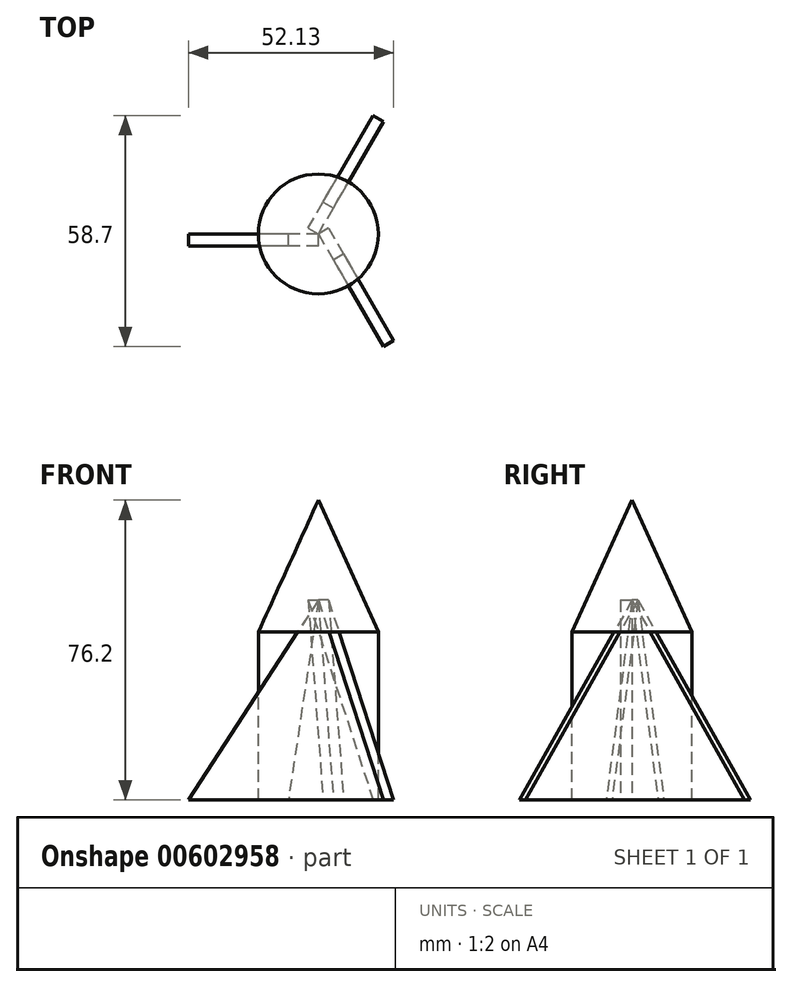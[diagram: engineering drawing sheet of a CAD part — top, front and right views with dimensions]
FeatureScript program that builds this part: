
annotation { "Feature Type Name" : "Feature", "Feature Type Description" : "" }
export const myFeature = defineFeature(function(context is Context, id is Id, definition is map)
    precondition{}
    {
        {
            var Q0;
            Q0=qCreatedBy(makeId("Front.planeOp"),FACE);
            var sketch = newSketch(context, id + "F0", { "sketchPlane" : qUnion([Q0])});
            skLineSegment(sketch, "E0", {"start": v(-15.24, 42.64) * mm, "end": v(-15.24, 0) * mm});
            skLineSegment(sketch, "E1", {"start": v(-15.24, 42.64) * mm, "end": v(0, 76.2) * mm});
            skLineSegment(sketch, "E2", {"start": v(0, 76.2) * mm, "end": v(0, 0) * mm});
            skLineSegment(sketch, "E3", {"start": v(-15.24, 0) * mm, "end": v(0, 0) * mm});
            skSolve(sketch);
        }
        {
            var Q0;
            Q0=makeQuery(id+"F0.imprint","IMPRINT",FACE,{"disambiguationData":[TD([[makeQuery(id+"F0.imprint","IMPRINT",EDGE,{"derivedFrom":sQuery(id+"F0.wireOp",EDGE,"E0")}),1.0]])]});
            var Q1;
            Q1=sQuery(id+"F0.wireOp",EDGE,"E2");
            revolve(context, id + "F1", {"entities" : qUnion([Q0]), "axis" : qUnion([Q1]), "revolveType" : RevolveType.FULL});
        }
        {
            var Q0;
            Q0=qCreatedBy(makeId("Front.planeOp"),FACE);
            var sketch = newSketch(context, id + "F2", { "sketchPlane" : qUnion([Q0])});
            skLineSegment(sketch, "E4", {"start": v(0, -12.68) * mm, "end": v(0, 76.93) * mm, "construction": true});
            skSolve(sketch);
        }
        {
            var Q0;
            Q0=qCreatedBy(makeId("Front.planeOp"),FACE);
            var sketch = newSketch(context, id + "F3", { "sketchPlane" : qUnion([Q0])});
            skLineSegment(sketch, "E5", {"start": v(0, 50.78) * mm, "end": v(-33.02, 0) * mm});
            skLineSegment(sketch, "E6", {"start": v(-7.62, 0) * mm, "end": v(-33.02, 0) * mm});
            skLineSegment(sketch, "E7", {"start": v(0, 50.78) * mm, "end": v(-7.62, 0) * mm});
            skSolve(sketch);
        }
        {
            var Q0;
            Q0=makeQuery(id+"F3.imprint","IMPRINT",FACE,{"disambiguationData":[TD([[makeQuery(id+"F3.imprint","IMPRINT",EDGE,{"derivedFrom":sQuery(id+"F3.wireOp",EDGE,"E5")}),1.0]])]});
            extrude(context, id + "F4", {"entities" : qUnion([Q0]), "depth" : 3 * mm, "offsetDistance" : 25.4 * mm});
        }
        {
            var Q0;
            Q0=makeQuery(id+"F4.opExtrude","SWEPT_BODY",BODY,{"disambiguationData":[OSD([sQuery(id+"F3.wireOp",EDGE,"E5"),sQuery(id+"F3.wireOp",EDGE,"E6"),sQuery(id+"F3.wireOp",EDGE,"E7")])]});
            var Q1;
            Q1=sQuery(id+"F2.wireOp",EDGE,"E4");
            circularPattern(context, id + "F5", {"entities" : qUnion([Q0]), "axis" : qUnion([Q1]), "angle" : 360 * degree, "instanceCount" : 3, "equalSpace" : true});
        }
    });
